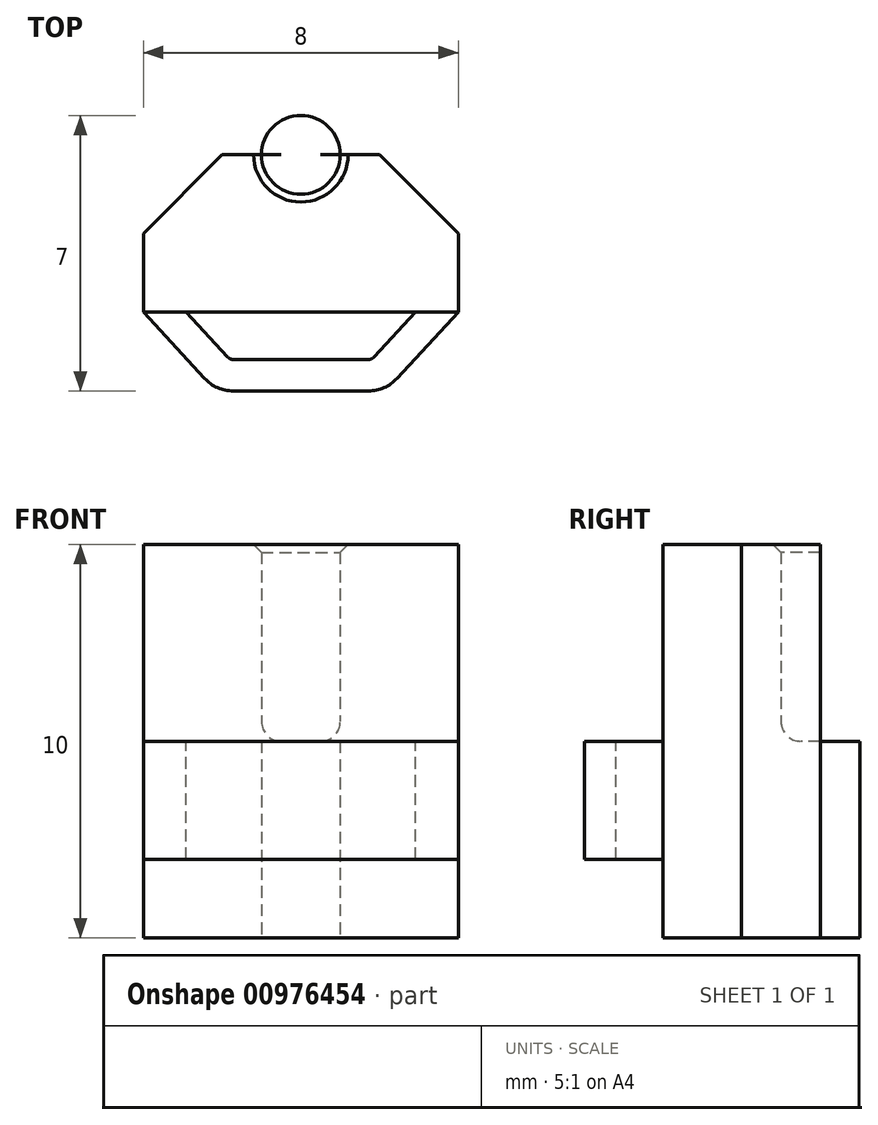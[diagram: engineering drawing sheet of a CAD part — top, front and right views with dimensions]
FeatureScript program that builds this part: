
annotation { "Feature Type Name" : "Feature", "Feature Type Description" : "" }
export const myFeature = defineFeature(function(context is Context, id is Id, definition is map)
    precondition{}
    {
        {
            var Q0;
            Q0=qCreatedBy(makeId("Top.planeOp"),FACE);
            var sketch = newSketch(context, id + "F0", { "sketchPlane" : qUnion([Q0])});
            skLineSegment(sketch, "E0", {"start": v(0, 0) * mm, "end": v(0, 2) * mm});
            skLineSegment(sketch, "E1", {"start": v(0, 2) * mm, "end": v(2, 4) * mm});
            skLineSegment(sketch, "E2", {"start": v(2, 4) * mm, "end": v(6, 4) * mm});
            skLineSegment(sketch, "E3", {"start": v(6, 4) * mm, "end": v(8, 2) * mm});
            skLineSegment(sketch, "E4", {"start": v(8, 2) * mm, "end": v(8, 0) * mm});
            skLineSegment(sketch, "E5", {"start": v(8, 0) * mm, "end": v(0, 0) * mm});
            skCircle(sketch, "E6", {"center": v(4, 4) * mm, "radius": 1 * mm});
            skSolve(sketch);
        }
        {
            var Q0;
            Q0 = qSketchRegion(id + "F0", true);
            extrude(context, id + "F1", {"entities" : qUnion([Q0]), "depth" : 5 * mm, "offsetDistance" : 25 * mm});
        }
        {
            var Q0;
            {var subQ0=sQuery(id+"F0.wireOp",EDGE,"E6");var subQ1=sQuery(id+"F0.wireOp",EDGE,"E2");var subQ2=makeQuery(id+"F0.imprint","INTERSECT",VERTEX,{"disambiguationData":[OD(0.0)],"derivedFrom":[subQ1,subQ0]});Q0=makeQuery(id+"F0.imprint","IMPRINT",FACE,{"disambiguationData":[TD([[makeQuery(id+"F0.imprint","IMPRINT",EDGE,{"disambiguationData":[TD([[subQ2,-1.0]])],"derivedFrom":subQ1}),1.0]])]});}
            var Q1;
            {var subQ0=sQuery(id+"F0.wireOp",EDGE,"E6");var subQ1=sQuery(id+"F0.wireOp",EDGE,"E2");var subQ2=makeQuery(id+"F0.imprint","INTERSECT",VERTEX,{"disambiguationData":[OD(0.0)],"derivedFrom":[subQ1,subQ0]});Q1=makeQuery(id+"F0.imprint","IMPRINT",FACE,{"disambiguationData":[TD([[makeQuery(id+"F0.imprint","IMPRINT",EDGE,{"disambiguationData":[TD([[subQ2,-1.0]])],"derivedFrom":subQ1}),-1.0]])]});}
            extrude(context, id + "F2", {"entities" : qUnion([Q0, Q1]), "operationType" : NewBodyOperationType.ADD, "depth" : 10 * mm, "offsetDistance" : 25 * mm});
        }
        {
            var Q0;
            Q0=makeQuery(id+"F2.opExtrude","CAP_EDGE",EDGE,{"disambiguationData":[OSD([sQuery(id+"F0.wireOp",EDGE,"E6")])],"isStart":false});
            chamfer(context, id + "F3", {"entities" : qUnion([Q0]), "width" : 0.2 * mm, "tangentPropagation" : true});
        }
        {
            var Q0;
            Q0=makeQuery(id+"F1.opExtrude","CAP_FACE",FACE,{"disambiguationData":[OSD([sQuery(id+"F0.wireOp",EDGE,"E0"),sQuery(id+"F0.wireOp",EDGE,"E1"),sQuery(id+"F0.wireOp",EDGE,"E2"),sQuery(id+"F0.wireOp",EDGE,"E3"),sQuery(id+"F0.wireOp",EDGE,"E4"),sQuery(id+"F0.wireOp",EDGE,"E5"),sQuery(id+"F0.wireOp",EDGE,"E6")])],"isStart":false});
            var sketch = newSketch(context, id + "F4", { "sketchPlane" : qUnion([Q0])});
            skLineSegment(sketch, "E7", {"start": v(0, 0) * mm, "end": v(1.55, -1.68) * mm});
            skLineSegment(sketch, "E8", {"start": v(2.29, -2) * mm, "end": v(5.71, -2) * mm});
            skLineSegment(sketch, "E9", {"start": v(6.45, -1.68) * mm, "end": v(8, 0) * mm});
            skLineSegment(sketch, "E10", {"start": v(4, -2) * mm, "end": v(4, 0) * mm, "construction": true});
            skPoint(sketch, "E11.visualSharp", {"position": v(1.85, -2) * mm});
            skArc(sketch, "E11.filletArc", {"start": v(1.55, -1.68) * mm, "mid": v(1.89, -1.92) * mm, "end": v(2.29, -2) * mm});
            skPoint(sketch, "E12.visualSharp", {"position": v(6.15, -2) * mm});
            skArc(sketch, "E12.filletArc", {"start": v(5.71, -2) * mm, "mid": v(6.11, -1.92) * mm, "end": v(6.45, -1.68) * mm});
            skLineSegment(sketch, "E13.0", {"start": v(5.86, -1.14) * mm, "end": v(6.91, 0) * mm});
            skLineSegment(sketch, "E13.1", {"start": v(1.09, 0) * mm, "end": v(2.14, -1.14) * mm});
            skArc(sketch, "E13.2", {"start": v(2.14, -1.14) * mm, "mid": v(2.2, -1.18) * mm, "end": v(2.29, -1.2) * mm});
            skLineSegment(sketch, "E13.3", {"start": v(2.29, -1.2) * mm, "end": v(5.71, -1.2) * mm});
            skArc(sketch, "E13.4", {"start": v(5.71, -1.2) * mm, "mid": v(5.8, -1.18) * mm, "end": v(5.86, -1.14) * mm});
            skLineSegment(sketch, "E14", {"start": v(0, 0) * mm, "end": v(8, 0) * mm});
            skSolve(sketch);
        }
        {
            var Q0;
            {var subQ2=sQuery(id+"F4.wireOp",EDGE,"E7");Q0=makeQuery(id+"F4.imprint","IMPRINT",FACE,{"disambiguationData":[TD([[makeQuery(id+"F4.imprint","IMPRINT",EDGE,{"derivedFrom":subQ2}),1.0]])]});}
            extrude(context, id + "F5", {"entities" : qUnion([Q0]), "operationType" : NewBodyOperationType.ADD, "oppositeDirection" : true, "depth" : 3 * mm, "offsetDistance" : 25 * mm});
        }
        {
            var Q0;
            {var subQ0=sQuery(id+"F4.wireOp",EDGE,"E14");Q0=makeQuery(id+"F5.opExtrude","CAP_EDGE",EDGE,{"disambiguationData":[OSD([subQ0]),TDD([makeQuery(id+"F4.imprint","IMPRINT",EDGE,{"disambiguationData":[TD([[makeQuery(id+"F4.imprint","INTERSECT",VERTEX,{"derivedFrom":[sQuery(id+"F4.wireOp",EDGE,"E13.0"),subQ0]}),1.0]])],"derivedFrom":subQ0})])],"isStart":false});}
            var Q1;
            {var subQ0=sQuery(id+"F4.wireOp",EDGE,"E14");Q1=makeQuery(id+"F5.opExtrude","CAP_EDGE",EDGE,{"disambiguationData":[OSD([subQ0]),TDD([makeQuery(id+"F4.imprint","IMPRINT",EDGE,{"disambiguationData":[TD([[makeQuery(id+"F4.imprint","INTERSECT",VERTEX,{"derivedFrom":[sQuery(id+"F4.wireOp",EDGE,"E13.1"),subQ0]}),-1.0]])],"derivedFrom":subQ0})])],"isStart":false});}
            var Q2;
            Q2=makeQuery(id+"F5.opExtrude","SWEPT_EDGE",EDGE,{"disambiguationData":[OSD([sQuery(id+"F4.wireOp",EDGE,"E13.0"),sQuery(id+"F4.wireOp",EDGE,"E14")])]});
            var Q3;
            Q3=makeQuery(id+"F5.opExtrude","SWEPT_EDGE",EDGE,{"disambiguationData":[OSD([sQuery(id+"F4.wireOp",EDGE,"E13.1"),sQuery(id+"F4.wireOp",EDGE,"E14")])]});
            var Q4;
            {var subQ0=sQuery(id+"F0.wireOp",EDGE,"E6");Q4=makeQuery(id+"F2.boolean.opBoolean","INTERSECT",EDGE,{"derivedFrom":[makeQuery(id+"F1.opExtrude","CAP_FACE",FACE,{"disambiguationData":[OSD([sQuery(id+"F0.wireOp",EDGE,"E0"),sQuery(id+"F0.wireOp",EDGE,"E1"),sQuery(id+"F0.wireOp",EDGE,"E2"),sQuery(id+"F0.wireOp",EDGE,"E3"),sQuery(id+"F0.wireOp",EDGE,"E4"),sQuery(id+"F0.wireOp",EDGE,"E5"),subQ0])],"isStart":false}),makeQuery(id+"F2.opExtrude","SWEPT_FACE",FACE,{"disambiguationData":[OSD([subQ0])]})]});}
            fillet(context, id + "F6", {"entities" : qUnion([Q0, Q1, Q2, Q3, Q4]), "radius" : 0.5 * mm, "tangentPropagation" : true, "allowEdgeOverflow" : false});
        }
    });
